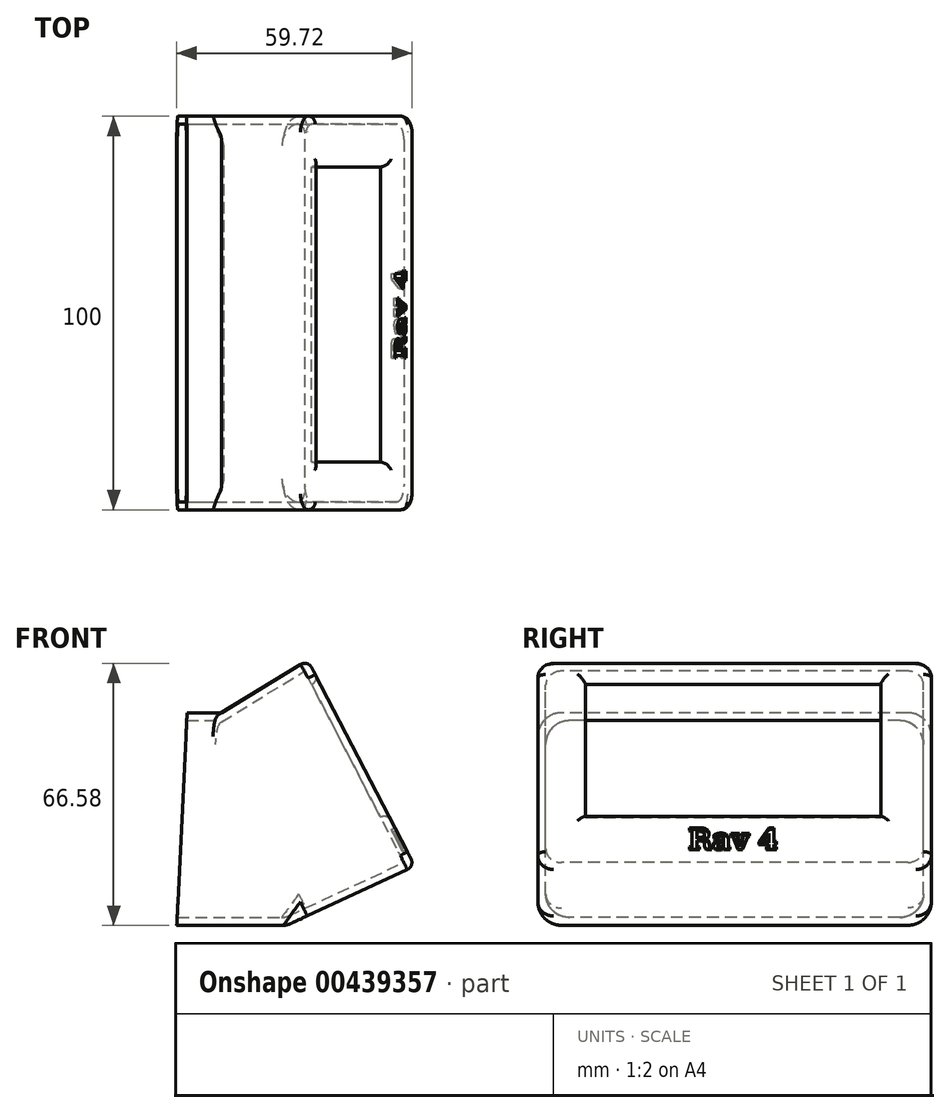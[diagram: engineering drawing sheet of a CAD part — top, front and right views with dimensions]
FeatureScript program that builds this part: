
annotation { "Feature Type Name" : "Feature", "Feature Type Description" : "" }
export const myFeature = defineFeature(function(context is Context, id is Id, definition is map)
    precondition{}
    {
        {
            var Q0;
            Q0=qCreatedBy(makeId("Front.planeOp"),FACE);
            var sketch = newSketch(context, id + "F0", { "sketchPlane" : qUnion([Q0])});
            skPoint(sketch, "E0.middle", {"position": v(0, 0) * mm});
            skLineSegment(sketch, "E1", {"start": v(-33.28, 0) * mm, "end": v(-33.28, 54) * mm});
            skLineSegment(sketch, "E2", {"start": v(-33.28, 54) * mm, "end": v(-21.94, 54) * mm});
            skLineSegment(sketch, "E3", {"start": v(-21.94, 54) * mm, "end": v(0, 67.4) * mm});
            skLineSegment(sketch, "E4", {"start": v(-33.28, 0) * mm, "end": v(-5.28, 0) * mm});
            skLineSegment(sketch, "E5", {"start": v(27.18, 15.04) * mm, "end": v(0, 67.4) * mm});
            skLineSegment(sketch, "E6", {"start": v(-5.28, 0) * mm, "end": v(27.18, 15.04) * mm});
            skSolve(sketch);
        }
        {
            var Q0;
            Q0=makeQuery(id+"F0.imprint","IMPRINT",FACE,{"disambiguationData":[TD([[makeQuery(id+"F0.imprint","IMPRINT",EDGE,{"derivedFrom":sQuery(id+"F0.wireOp",EDGE,"E1")}),-1.0]])]});
            extrude(context, id + "F1", {"entities" : qUnion([Q0]), "oppositeDirection" : true, "depth" : 100 * mm});
        }
        {
            var Q0;
            Q0=makeQuery(id+"F1.opExtrude","SWEPT_FACE",FACE,{"disambiguationData":[OSD([sQuery(id+"F0.wireOp",EDGE,"E5")])]});
            var sketch = newSketch(context, id + "F2", { "sketchPlane" : qUnion([Q0])});
            skLineSegment(sketch, "E7.bottom", {"start": v(14.1, 51.83) * mm, "end": v(85.1, 51.83) * mm});
            skLineSegment(sketch, "E7.top", {"start": v(14.1, 17.83) * mm, "end": v(85.1, 17.83) * mm});
            skLineSegment(sketch, "E7.left", {"start": v(14.1, 51.83) * mm, "end": v(14.1, 17.83) * mm});
            skLineSegment(sketch, "E7.right", {"start": v(85.1, 51.83) * mm, "end": v(85.1, 17.83) * mm});
            skSolve(sketch);
        }
        {
            var Q0;
            Q0 = qSketchRegion(id + "F2", true);
            extrude(context, id + "F3", {"entities" : qUnion([Q0]), "operationType" : NewBodyOperationType.REMOVE, "oppositeDirection" : true, "depth" : 1 * mm});
        }
        {
            var Q0;
            Q0=makeQuery(id+"F1.opExtrude","SWEPT_FACE",FACE,{"disambiguationData":[OSD([sQuery(id+"F0.wireOp",EDGE,"E1")])]});
            shell(context, id + "F4", {"entities" : qUnion([Q0]), "thickness" : 2 * mm});
        }
        {
            var Q0;
            Q0=makeQuery(id+"F4.opShell","OFFSET_FACE",FACE,{"disambiguationData":[OSD([sQuery(id+"F2.wireOp",EDGE,"E7.bottom"),sQuery(id+"F2.wireOp",EDGE,"E7.top"),sQuery(id+"F2.wireOp",EDGE,"E7.left"),sQuery(id+"F2.wireOp",EDGE,"E7.right")])]});
            extrude(context, id + "F5", {"entities" : qUnion([Q0]), "operationType" : NewBodyOperationType.REMOVE, "oppositeDirection" : true, "depth" : 25 * mm});
        }
        {
            var Q0;
            Q0=makeQuery(id+"F1.opExtrude","CAP_EDGE",EDGE,{"disambiguationData":[OSD([sQuery(id+"F0.wireOp",EDGE,"E2")])],"isStart":true});
            fillet(context, id + "F6", {"entities" : qUnion([Q0]), "radius" : 6 * mm, "tangentPropagation" : true, "allowEdgeOverflow" : false});
        }
        {
            var Q0;
            Q0=makeQuery(id+"F1.opExtrude","CAP_EDGE",EDGE,{"disambiguationData":[OSD([sQuery(id+"F0.wireOp",EDGE,"E4")])],"isStart":true});
            var Q1;
            Q1=makeQuery(id+"F1.opExtrude","CAP_EDGE",EDGE,{"disambiguationData":[OSD([sQuery(id+"F0.wireOp",EDGE,"E4")])],"isStart":false});
            var Q2;
            Q2=makeQuery(id+"F1.opExtrude","CAP_EDGE",EDGE,{"disambiguationData":[OSD([sQuery(id+"F0.wireOp",EDGE,"E2")])],"isStart":false});
            fillet(context, id + "F7", {"entities" : qUnion([Q0, Q1, Q2]), "radius" : 6 * mm, "tangentPropagation" : true, "allowEdgeOverflow" : false});
        }
        {
            var Q0;
            Q0=makeQuery(id+"F1.opExtrude","CAP_EDGE",EDGE,{"disambiguationData":[OSD([sQuery(id+"F0.wireOp",EDGE,"E3")])],"isStart":false});
            fillet(context, id + "F8", {"entities" : qUnion([Q0]), "radius" : 4 * mm, "tangentPropagation" : true, "allowEdgeOverflow" : false});
        }
        {
            var Q0;
            Q0=makeQuery(id+"F1.opExtrude","CAP_EDGE",EDGE,{"disambiguationData":[OSD([sQuery(id+"F0.wireOp",EDGE,"E6")])],"isStart":false});
            var Q1;
            Q1=makeQuery(id+"F1.opExtrude","CAP_EDGE",EDGE,{"disambiguationData":[OSD([sQuery(id+"F0.wireOp",EDGE,"E3")])],"isStart":true});
            fillet(context, id + "F9", {"entities" : qUnion([Q0, Q1]), "radius" : 4 * mm, "tangentPropagation" : true, "allowEdgeOverflow" : false});
        }
        {
            var Q0;
            Q0=makeQuery(id+"F1.opExtrude","SWEPT_FACE",FACE,{"disambiguationData":[OSD([sQuery(id+"F0.wireOp",EDGE,"E5")])]});
            fillet(context, id + "F10", {"entities" : qUnion([Q0]), "radius" : 2 * mm, "tangentPropagation" : true, "allowEdgeOverflow" : false});
        }
        {
            var Q0;
            {var subQ0=sQuery(id+"F0.wireOp",EDGE,"E2");Q0=makeQuery(id+"F4.opShell","OFFSET_EDGE",EDGE,{"disambiguationData":[OSD([subQ0]),TDD([makeQuery(id+"F1.opExtrude","CAP_EDGE",EDGE,{"disambiguationData":[OSD([subQ0])],"isStart":true})])]});}
            var Q1;
            {var subQ0=sQuery(id+"F0.wireOp",EDGE,"E4");Q1=makeQuery(id+"F4.opShell","OFFSET_EDGE",EDGE,{"disambiguationData":[OSD([subQ0]),TDD([makeQuery(id+"F1.opExtrude","CAP_EDGE",EDGE,{"disambiguationData":[OSD([subQ0])],"isStart":true})])]});}
            var Q2;
            {var subQ0=sQuery(id+"F0.wireOp",EDGE,"E4");Q2=makeQuery(id+"F4.opShell","OFFSET_EDGE",EDGE,{"disambiguationData":[OSD([subQ0]),TDD([makeQuery(id+"F1.opExtrude","CAP_EDGE",EDGE,{"disambiguationData":[OSD([subQ0])],"isStart":false})])]});}
            var Q3;
            {var subQ0=sQuery(id+"F0.wireOp",EDGE,"E2");Q3=makeQuery(id+"F4.opShell","OFFSET_EDGE",EDGE,{"disambiguationData":[OSD([subQ0]),TDD([makeQuery(id+"F1.opExtrude","CAP_EDGE",EDGE,{"disambiguationData":[OSD([subQ0])],"isStart":false})])]});}
            fillet(context, id + "F11", {"entities" : qUnion([Q0, Q1, Q2, Q3]), "radius" : 6 * mm, "tangentPropagation" : true, "allowEdgeOverflow" : false});
        }
        {
            var Q0;
            {var subQ0=sQuery(id+"F0.wireOp",EDGE,"E6");Q0=makeQuery(id+"F4.opShell","OFFSET_EDGE",EDGE,{"disambiguationData":[OSD([subQ0]),TDD([makeQuery(id+"F1.opExtrude","CAP_EDGE",EDGE,{"disambiguationData":[OSD([subQ0])],"isStart":true})])]});}
            var Q1;
            {var subQ0=sQuery(id+"F0.wireOp",EDGE,"E3");Q1=makeQuery(id+"F4.opShell","OFFSET_EDGE",EDGE,{"disambiguationData":[OSD([subQ0]),TDD([makeQuery(id+"F1.opExtrude","CAP_EDGE",EDGE,{"disambiguationData":[OSD([subQ0])],"isStart":true})])]});}
            var Q2;
            {var subQ0=sQuery(id+"F0.wireOp",EDGE,"E3");Q2=makeQuery(id+"F4.opShell","OFFSET_EDGE",EDGE,{"disambiguationData":[OSD([subQ0]),TDD([makeQuery(id+"F1.opExtrude","CAP_EDGE",EDGE,{"disambiguationData":[OSD([subQ0])],"isStart":false})])]});}
            fillet(context, id + "F12", {"entities" : qUnion([Q0, Q1, Q2]), "radius" : 4 * mm, "tangentPropagation" : true, "allowEdgeOverflow" : false});
        }
        {
            var Q0;
            Q0=makeQuery(id+"F1.opExtrude","SWEPT_FACE",FACE,{"disambiguationData":[OSD([sQuery(id+"F0.wireOp",EDGE,"E5")])]});
            var sketch = newSketch(context, id + "F13", { "sketchPlane" : qUnion([Q0])});
            skText(sketch, "E8", { "text": "Rav 4", "fontName": "RobotoSlab-Bold.ttf"});
            const initialGuessF13  = {"E8": [0.0383, 0.00565, 1, 0, 0.00622]};
            skSetInitialGuess(sketch, initialGuessF13);
            skSolve(sketch);
        }
        {
            var Q0;
            Q0 = qSketchRegion(id + "F13", true);
            extrude(context, id + "F14", {"entities" : qUnion([Q0]), "operationType" : NewBodyOperationType.REMOVE, "oppositeDirection" : true, "depth" : 1 * mm});
        }
        {
            var Q0;
            Q0=makeQuery(id+"F1.opExtrude","CAP_FACE",FACE,{"disambiguationData":[OSD([sQuery(id+"F0.wireOp",EDGE,"E1"),sQuery(id+"F0.wireOp",EDGE,"E2"),sQuery(id+"F0.wireOp",EDGE,"E3"),sQuery(id+"F0.wireOp",EDGE,"E4"),sQuery(id+"F0.wireOp",EDGE,"E5"),sQuery(id+"F0.wireOp",EDGE,"E6")])],"isStart":true});
            var sketch = newSketch(context, id + "F15", { "sketchPlane" : qUnion([Q0])});
            skLineSegment(sketch, "E9", {"start": v(-33.27, 0) * mm, "end": v(-30.63, 54.66) * mm});
            skLineSegment(sketch, "E10", {"start": v(-30.63, 54.66) * mm, "end": v(-35.56, 54.9) * mm});
            skLineSegment(sketch, "E11", {"start": v(-35.56, 54.9) * mm, "end": v(-33.27, 0) * mm});
            skSolve(sketch);
        }
        {
            var Q0;
            Q0 = qSketchRegion(id + "F15", true);
            extrude(context, id + "F16", {"entities" : qUnion([Q0]), "operationType" : NewBodyOperationType.REMOVE, "endBound" : BoundingType.THROUGH_ALL, "oppositeDirection" : true, "depth" : 25 * mm});
        }
    });
